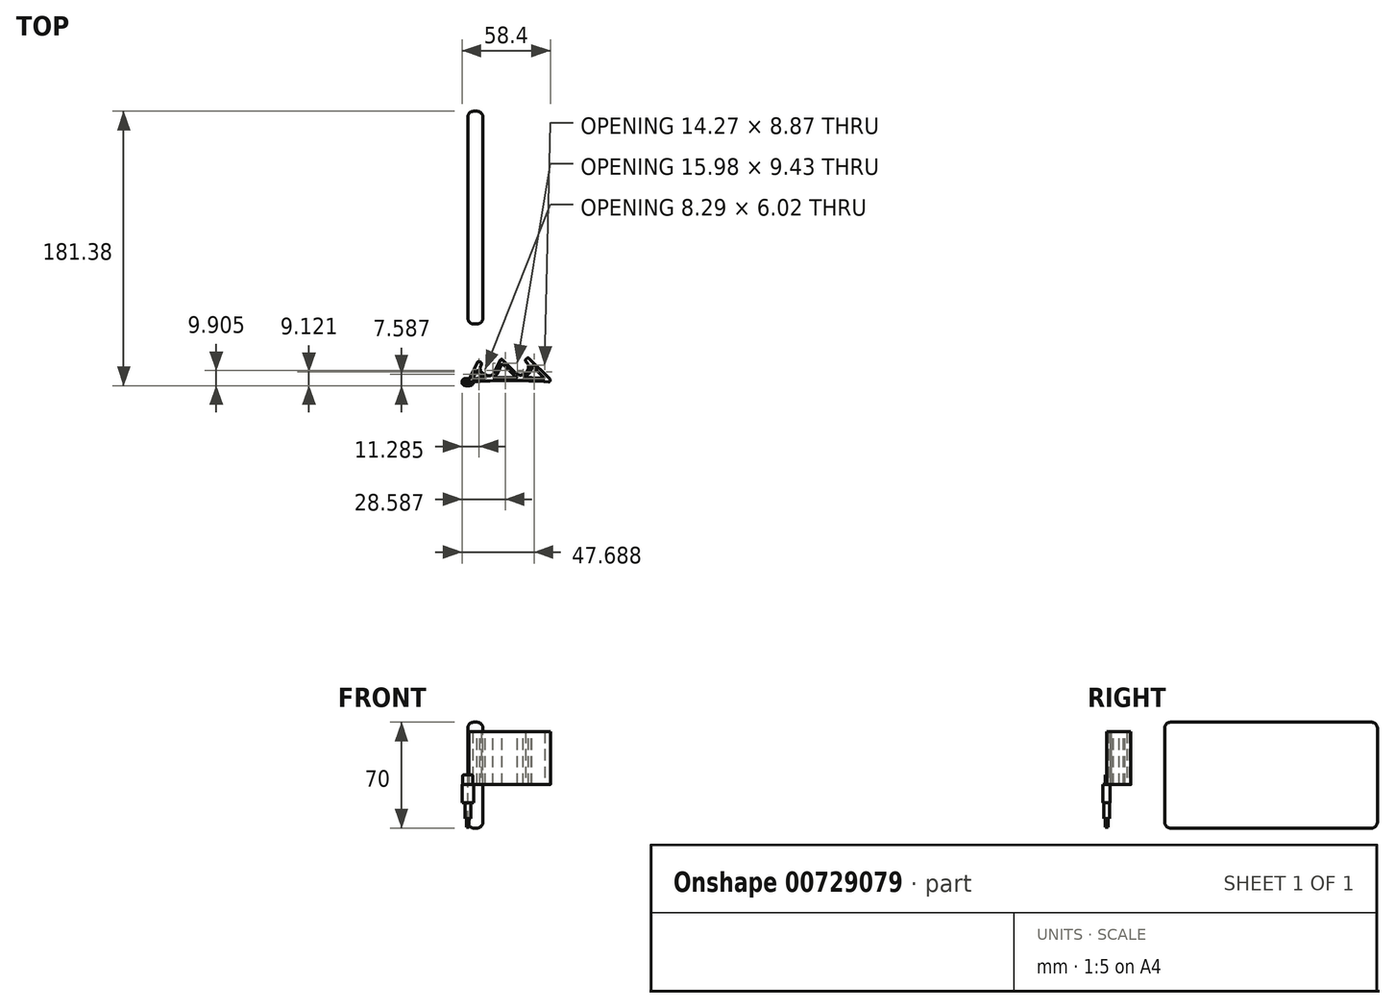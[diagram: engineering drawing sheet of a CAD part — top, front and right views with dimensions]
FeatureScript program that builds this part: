
annotation { "Feature Type Name" : "Feature", "Feature Type Description" : "" }
export const myFeature = defineFeature(function(context is Context, id is Id, definition is map)
    precondition{}
    {
        {
            var Q0;
            Q0=qCreatedBy(makeId("Right.planeOp"),FACE);
            var sketch = newSketch(context, id + "F0", { "sketchPlane" : qUnion([Q0])});
            skLineSegment(sketch, "E0.bottom", {"start": v(38.43, -28.68) * mm, "end": v(179.03, -28.68) * mm});
            skLineSegment(sketch, "E0.top", {"start": v(38.43, 41.32) * mm, "end": v(179.03, 41.32) * mm});
            skLineSegment(sketch, "E0.left", {"start": v(38.43, -28.68) * mm, "end": v(38.43, 41.32) * mm});
            skLineSegment(sketch, "E0.right", {"start": v(179.03, -28.68) * mm, "end": v(179.03, 41.32) * mm});
            skSolve(sketch);
        }
        {
            var Q0;
            Q0 = qSketchRegion(id + "F0", true);
            extrude(context, id + "F1", {"entities" : qUnion([Q0]), "depth" : 10 * mm, "offsetDistance" : 25 * mm});
        }
        {
            var Q0;
            Q0=makeQuery(id+"F1.opExtrude","CAP_FACE",FACE,{"disambiguationData":[OSD([sQuery(id+"F0.wireOp",EDGE,"E0.bottom"),sQuery(id+"F0.wireOp",EDGE,"E0.top"),sQuery(id+"F0.wireOp",EDGE,"E0.left"),sQuery(id+"F0.wireOp",EDGE,"E0.right")])],"isStart":true});
            var Q1;
            Q1=makeQuery(id+"F1.opExtrude","CAP_FACE",FACE,{"disambiguationData":[OSD([sQuery(id+"F0.wireOp",EDGE,"E0.bottom"),sQuery(id+"F0.wireOp",EDGE,"E0.top"),sQuery(id+"F0.wireOp",EDGE,"E0.left"),sQuery(id+"F0.wireOp",EDGE,"E0.right")])],"isStart":false});
            var Q2;
            Q2=makeQuery(id+"F1.opExtrude","SWEPT_EDGE",EDGE,{"disambiguationData":[OSD([sQuery(id+"F0.wireOp",EDGE,"E0.top"),sQuery(id+"F0.wireOp",EDGE,"E0.left")])]});
            var Q3;
            Q3=makeQuery(id+"F1.opExtrude","SWEPT_EDGE",EDGE,{"disambiguationData":[OSD([sQuery(id+"F0.wireOp",EDGE,"E0.bottom"),sQuery(id+"F0.wireOp",EDGE,"E0.left")])]});
            var Q4;
            Q4=makeQuery(id+"F1.opExtrude","SWEPT_EDGE",EDGE,{"disambiguationData":[OSD([sQuery(id+"F0.wireOp",EDGE,"E0.bottom"),sQuery(id+"F0.wireOp",EDGE,"E0.right")])]});
            var Q5;
            Q5=makeQuery(id+"F1.opExtrude","SWEPT_EDGE",EDGE,{"disambiguationData":[OSD([sQuery(id+"F0.wireOp",EDGE,"E0.top"),sQuery(id+"F0.wireOp",EDGE,"E0.right")])]});
            fillet(context, id + "F2", {"entities" : qUnion([Q0, Q1, Q2, Q3, Q4, Q5]), "radius" : 4 * mm, "tangentPropagation" : true, "allowEdgeOverflow" : false});
        }
        {
            var Q0;
            Q0=qCreatedBy(makeId("Top.planeOp"),FACE);
            var sketch = newSketch(context, id + "F3", { "sketchPlane" : qUnion([Q0])});
            skLineSegment(sketch, "E1", {"start": v(56.16, 0) * mm, "end": v(39.78, 16.38) * mm});
            skLineSegment(sketch, "E2", {"start": v(39.78, 16.38) * mm, "end": v(37.66, 14.26) * mm});
            skLineSegment(sketch, "E3", {"start": v(37.66, 14.26) * mm, "end": v(41.9, 10.01) * mm});
            skLineSegment(sketch, "E4", {"start": v(41.9, 10.01) * mm, "end": v(34.83, 2.94) * mm});
            skLineSegment(sketch, "E5", {"start": v(34.83, 2.94) * mm, "end": v(22.1, 15.67) * mm});
            skLineSegment(sketch, "E6", {"start": v(22.1, 15.67) * mm, "end": v(15.83, 2.81) * mm});
            skLineSegment(sketch, "E7", {"start": v(15.83, 2.81) * mm, "end": v(6.85, 7.2) * mm});
            skLineSegment(sketch, "E8", {"start": v(6.85, 7.2) * mm, "end": v(9.48, 12.59) * mm});
            skLineSegment(sketch, "E9", {"start": v(9.48, 12.59) * mm, "end": v(6.78, 13.9) * mm});
            skLineSegment(sketch, "E10", {"start": v(6.78, 13.9) * mm, "end": v(0, 0) * mm});
            skLineSegment(sketch, "E11", {"start": v(22.1, 15.67) * mm, "end": v(22.1, 0) * mm, "construction": true});
            skLineSegment(sketch, "E12", {"start": v(15.83, 2.81) * mm, "end": v(77.47, 129.18) * mm, "construction": true});
            skLineSegment(sketch, "E13", {"start": v(15.83, 2.81) * mm, "end": v(6.85, 7.2) * mm, "construction": true});
            skLineSegment(sketch, "E14", {"start": v(6.85, 7.2) * mm, "end": v(68.48, 133.57) * mm, "construction": true});
            skLineSegment(sketch, "E15", {"start": v(68.48, 133.57) * mm, "end": v(77.47, 129.18) * mm, "construction": true});
            skLineSegment(sketch, "E16", {"start": v(34.83, 2.94) * mm, "end": v(-14.67, 52.44) * mm, "construction": true});
            skLineSegment(sketch, "E17", {"start": v(34.83, 2.94) * mm, "end": v(41.9, 10.01) * mm, "construction": true});
            skLineSegment(sketch, "E18", {"start": v(41.9, 10.01) * mm, "end": v(-7.6, 59.51) * mm, "construction": true});
            skLineSegment(sketch, "E19", {"start": v(-7.6, 59.51) * mm, "end": v(-14.67, 52.44) * mm, "construction": true});
            skLineSegment(sketch, "E20", {"start": v(56.16, 0) * mm, "end": v(56.16, 85.49) * mm, "construction": true});
            skPoint(sketch, "E20.endSnap0", {"position": v(72.98, 131.37) * mm});
            skLineSegment(sketch, "E21", {"start": v(37.66, 70.38) * mm, "end": v(46.65, 66) * mm, "construction": true});
            skLineSegment(sketch, "E22", {"start": v(42.16, 68.19) * mm, "end": v(42.16, 0) * mm, "construction": true});
            skArc(sketch, "E23", {"start": v(56.16, 0) * mm, "mid": v(28.08, 1) * mm, "end": v(0, 0) * mm});
            skLineSegment(sketch, "E24", {"start": v(0, 0) * mm, "end": v(56.16, 0) * mm, "construction": true});
            skLineSegment(sketch, "E25", {"start": v(0.75, 0.7) * mm, "end": v(0.75, 5.95) * mm, "construction": true});
            skPoint(sketch, "E26", {"position": v(18.94, 31.2) * mm});
            skLineSegment(sketch, "E27", {"start": v(56.16, 0) * mm, "end": v(42.16, 68.19) * mm, "construction": true});
            skSolve(sketch);
        }
        {
            var Q0;
            {var subQ5=sQuery(id+"F3.wireOp",EDGE,"E2");Q0=makeQuery(id+"F3.imprint","IMPRINT",FACE,{"disambiguationData":[TD([[makeQuery(id+"F3.imprint","IMPRINT",EDGE,{"derivedFrom":subQ5}),1.0]])]});}
            var Q1;
            {var subQ0=sQuery(id+"F3.wireOp",EDGE,"E1");var subQ1=sQuery(id+"F3.wireOp",EDGE,"3Ye0FZxl-FkT7-tVTo-dLDi-VFVJxXrmrOT7");var subQ2=makeQuery(id+"F3.imprint","INTERSECT",VERTEX,{"derivedFrom":[subQ1,subQ0]});Q1=makeQuery(id+"F3.imprint","IMPRINT",FACE,{"disambiguationData":[TD([[makeQuery(id+"F3.imprint","IMPRINT",EDGE,{"disambiguationData":[TD([[subQ2,1.0]])],"derivedFrom":subQ1}),-1.0]])]});}
            var Q2;
            {var subQ0=sQuery(id+"F3.wireOp",EDGE,"E10");var subQ1=sQuery(id+"F3.wireOp",EDGE,"3Ye0FZxl-FkT7-tVTo-dLDi-VFVJxXrmrOT7");var subQ2=makeQuery(id+"F3.imprint","INTERSECT",VERTEX,{"derivedFrom":[subQ1,subQ0]});Q2=makeQuery(id+"F3.imprint","IMPRINT",FACE,{"disambiguationData":[TD([[makeQuery(id+"F3.imprint","IMPRINT",EDGE,{"disambiguationData":[TD([[subQ2,-1.0]])],"derivedFrom":subQ1}),-1.0]])]});}
            extrude(context, id + "F4", {"entities" : qUnion([Q0, Q1, Q2]), "depth" : 35 * mm, "offsetDistance" : 25 * mm});
        }
        {
            var Q0;
            Q0=makeQuery(id+"F4.opExtrude","SWEPT_EDGE",EDGE,{"disambiguationData":[OSD([sQuery(id+"F3.wireOp",EDGE,"E6"),sQuery(id+"F3.wireOp",EDGE,"E7")])]});
            var Q1;
            Q1=makeQuery(id+"F4.opExtrude","SWEPT_EDGE",EDGE,{"disambiguationData":[OSD([sQuery(id+"F3.wireOp",EDGE,"E4"),sQuery(id+"F3.wireOp",EDGE,"E5")])]});
            var Q2;
            Q2=makeQuery(id+"F4.opExtrude","SWEPT_EDGE",EDGE,{"disambiguationData":[OSD([sQuery(id+"F3.wireOp",EDGE,"E3"),sQuery(id+"F3.wireOp",EDGE,"E4")])]});
            var Q3;
            Q3=makeQuery(id+"F4.opExtrude","SWEPT_EDGE",EDGE,{"disambiguationData":[OSD([sQuery(id+"F3.wireOp",EDGE,"E7"),sQuery(id+"F3.wireOp",EDGE,"E8")])]});
            fillet(context, id + "F5", {"entities" : qUnion([Q0, Q1, Q2, Q3]), "radius" : 4 * mm, "tangentPropagation" : true, "allowEdgeOverflow" : false});
        }
        {
            var Q0;
            Q0=makeQuery(id+"F4.opExtrude","SWEPT_EDGE",EDGE,{"disambiguationData":[OSD([sQuery(id+"F3.wireOp",EDGE,"E2"),sQuery(id+"F3.wireOp",EDGE,"E3")])]});
            var Q1;
            Q1=makeQuery(id+"F4.opExtrude","SWEPT_EDGE",EDGE,{"disambiguationData":[OSD([sQuery(id+"F3.wireOp",EDGE,"E8"),sQuery(id+"F3.wireOp",EDGE,"E9")])]});
            var Q2;
            Q2=makeQuery(id+"F4.opExtrude","SWEPT_EDGE",EDGE,{"disambiguationData":[OSD([sQuery(id+"F3.wireOp",EDGE,"E1"),sQuery(id+"F3.wireOp",EDGE,"E2")])]});
            var Q3;
            Q3=makeQuery(id+"F4.opExtrude","SWEPT_EDGE",EDGE,{"disambiguationData":[OSD([sQuery(id+"F3.wireOp",EDGE,"E9"),sQuery(id+"F3.wireOp",EDGE,"E10")])]});
            var Q4;
            Q4=makeQuery(id+"F4.opExtrude","SWEPT_EDGE",EDGE,{"disambiguationData":[OSD([sQuery(id+"F3.wireOp",EDGE,"3Ye0FZxl-FkT7-tVTo-dLDi-VFVJxXrmrOT7"),sQuery(id+"F3.wireOp",EDGE,"E1")])]});
            var Q5;
            Q5=makeQuery(id+"F4.opExtrude","SWEPT_EDGE",EDGE,{"disambiguationData":[OSD([sQuery(id+"F3.wireOp",EDGE,"3Ye0FZxl-FkT7-tVTo-dLDi-VFVJxXrmrOT7"),sQuery(id+"F3.wireOp",EDGE,"E10")])]});
            var Q6;
            Q6=makeQuery(id+"F4.opExtrude","SWEPT_EDGE",EDGE,{"disambiguationData":[OSD([sQuery(id+"F3.wireOp",EDGE,"E5"),sQuery(id+"F3.wireOp",EDGE,"E6")])]});
            fillet(context, id + "F6", {"entities" : qUnion([Q0, Q1, Q2, Q3, Q4, Q5, Q6]), "radius" : 1 * mm, "tangentPropagation" : true, "allowEdgeOverflow" : false});
        }
        {
            var Q0;
            Q0=makeQuery(id+"F4.opExtrude","CAP_FACE",FACE,{"disambiguationData":[OSD([sQuery(id+"F3.wireOp",EDGE,"3Ye0FZxl-FkT7-tVTo-dLDi-VFVJxXrmrOT7"),sQuery(id+"F3.wireOp",EDGE,"E1"),sQuery(id+"F3.wireOp",EDGE,"E2"),sQuery(id+"F3.wireOp",EDGE,"E3"),sQuery(id+"F3.wireOp",EDGE,"E4"),sQuery(id+"F3.wireOp",EDGE,"E5"),sQuery(id+"F3.wireOp",EDGE,"E6"),sQuery(id+"F3.wireOp",EDGE,"E7"),sQuery(id+"F3.wireOp",EDGE,"E8"),sQuery(id+"F3.wireOp",EDGE,"E9"),sQuery(id+"F3.wireOp",EDGE,"E10")])],"isStart":false});
            var Q1;
            Q1=makeQuery(id+"F4.opExtrude","CAP_FACE",FACE,{"disambiguationData":[OSD([sQuery(id+"F3.wireOp",EDGE,"3Ye0FZxl-FkT7-tVTo-dLDi-VFVJxXrmrOT7"),sQuery(id+"F3.wireOp",EDGE,"E1"),sQuery(id+"F3.wireOp",EDGE,"E2"),sQuery(id+"F3.wireOp",EDGE,"E3"),sQuery(id+"F3.wireOp",EDGE,"E4"),sQuery(id+"F3.wireOp",EDGE,"E5"),sQuery(id+"F3.wireOp",EDGE,"E6"),sQuery(id+"F3.wireOp",EDGE,"E7"),sQuery(id+"F3.wireOp",EDGE,"E8"),sQuery(id+"F3.wireOp",EDGE,"E9"),sQuery(id+"F3.wireOp",EDGE,"E10")])],"isStart":true});
            shell(context, id + "F7", {"entities" : qUnion([Q0, Q1]), "thickness" : 2 * mm});
        }
        {
            var Q0;
            Q0=qCreatedBy(makeId("Top.planeOp"),FACE);
            var sketch = newSketch(context, id + "F8", { "sketchPlane" : qUnion([Q0])});
            skLineSegment(sketch, "E28.bottom", {"start": v(1.49, -2.35) * mm, "end": v(-1.48, -2.35) * mm});
            skLineSegment(sketch, "E28.top", {"start": v(1.48, 2.35) * mm, "end": v(-1.48, 2.35) * mm});
            skLineSegment(sketch, "E28.left", {"start": v(3.83, 0) * mm, "end": v(3.83, 0) * mm});
            skLineSegment(sketch, "E28.right", {"start": v(-3.83, 0) * mm, "end": v(-3.83, 0) * mm});
            skPoint(sketch, "E28.middle", {"position": v(0, 0) * mm});
            skLineSegment(sketch, "E29.bottom", {"start": v(3.35, -0.75) * mm, "end": v(-3.35, -0.76) * mm});
            skLineSegment(sketch, "E29.top", {"start": v(3.35, 0.76) * mm, "end": v(-3.35, 0.75) * mm});
            skLineSegment(sketch, "E29.left", {"start": v(3.35, -0.75) * mm, "end": v(3.35, 0.76) * mm});
            skLineSegment(sketch, "E29.right", {"start": v(-3.35, -0.76) * mm, "end": v(-3.35, 0.75) * mm});
            skPoint(sketch, "E30.visualSharp", {"position": v(-3.83, 2.35) * mm});
            skArc(sketch, "E30.filletArc", {"start": v(-1.48, 2.35) * mm, "mid": v(-3.15, 1.66) * mm, "end": v(-3.83, 0) * mm});
            skPoint(sketch, "E31.visualSharp", {"position": v(-3.83, -2.35) * mm});
            skArc(sketch, "E31.filletArc", {"start": v(-3.83, 0) * mm, "mid": v(-3.15, -1.66) * mm, "end": v(-1.48, -2.35) * mm});
            skPoint(sketch, "E32.visualSharp", {"position": v(3.83, -2.35) * mm});
            skArc(sketch, "E32.filletArc", {"start": v(1.49, -2.35) * mm, "mid": v(3.15, -1.66) * mm, "end": v(3.83, 0) * mm});
            skPoint(sketch, "E33.visualSharp", {"position": v(3.83, 2.35) * mm});
            skArc(sketch, "E33.filletArc", {"start": v(3.83, 0) * mm, "mid": v(3.15, 1.66) * mm, "end": v(1.48, 2.35) * mm});
            skSolve(sketch);
        }
        {
            var Q0;
            Q0 = qSketchRegion(id + "F8", true);
            var Q1;
            Q1=makeQuery(id+"F8.imprint","IMPRINT",FACE,{"disambiguationData":[TD([[makeQuery(id+"F8.imprint","IMPRINT",EDGE,{"derivedFrom":sQuery(id+"F8.wireOp",EDGE,"E29.bottom")}),-1.0]])]});
            extrude(context, id + "F9", {"entities" : qUnion([Q0, Q1]), "oppositeDirection" : true, "depth" : 12 * mm, "offsetDistance" : 25 * mm});
        }
        {
            var Q0;
            Q0=makeQuery(id+"F8.imprint","IMPRINT",FACE,{"disambiguationData":[TD([[makeQuery(id+"F8.imprint","IMPRINT",EDGE,{"derivedFrom":sQuery(id+"F8.wireOp",EDGE,"E29.bottom")}),-1.0]])]});
            extrude(context, id + "F10", {"entities" : qUnion([Q0]), "operationType" : NewBodyOperationType.ADD, "depth" : 6.55 * mm, "offsetDistance" : 25 * mm});
        }
        {
            var Q0;
            Q0=makeQuery(id+"F10.opExtrude","CAP_EDGE",EDGE,{"disambiguationData":[OSD([sQuery(id+"F8.wireOp",EDGE,"E29.right")])],"isStart":false});
            var Q1;
            Q1=makeQuery(id+"F10.opExtrude","CAP_EDGE",EDGE,{"disambiguationData":[OSD([sQuery(id+"F8.wireOp",EDGE,"E29.left")])],"isStart":false});
            fillet(context, id + "F11", {"entities" : qUnion([Q0, Q1]), "radius" : 1 * mm, "tangentPropagation" : true, "allowEdgeOverflow" : false});
        }
        {
            var Q0;
            Q0=makeQuery(id+"F9.opExtrude","CAP_FACE",FACE,{"disambiguationData":[OSD([sQuery(id+"F8.wireOp",EDGE,"E28.bottom"),sQuery(id+"F8.wireOp",EDGE,"E28.top"),sQuery(id+"F8.wireOp",EDGE,"E30.filletArc"),sQuery(id+"F8.wireOp",EDGE,"E31.filletArc"),sQuery(id+"F8.wireOp",EDGE,"E32.filletArc"),sQuery(id+"F8.wireOp",EDGE,"E33.filletArc")])],"isStart":false});
            var sketch = newSketch(context, id + "F12", { "sketchPlane" : qUnion([Q0])});
            skCircle(sketch, "E34", {"center": v(0, 0) * mm, "radius": 1.93 * mm});
            skSolve(sketch);
        }
        {
            var Q0;
            Q0 = qSketchRegion(id + "F12", true);
            extrude(context, id + "F13", {"entities" : qUnion([Q0]), "operationType" : NewBodyOperationType.ADD, "depth" : 10.3 * mm, "offsetDistance" : 25 * mm});
        }
        {
            var Q0;
            Q0=makeQuery(id+"F13.opExtrude","CAP_FACE",FACE,{"disambiguationData":[OSD([sQuery(id+"F12.wireOp",EDGE,"E34")])],"isStart":false});
            var sketch = newSketch(context, id + "F14", { "sketchPlane" : qUnion([Q0])});
            skCircle(sketch, "E35", {"center": v(0, 0) * mm, "radius": 0.9 * mm});
            skSolve(sketch);
        }
        {
            var Q0;
            Q0 = qSketchRegion(id + "F14", true);
            extrude(context, id + "F15", {"entities" : qUnion([Q0]), "operationType" : NewBodyOperationType.ADD, "depth" : 5.9 * mm, "offsetDistance" : 25 * mm});
        }
    });
